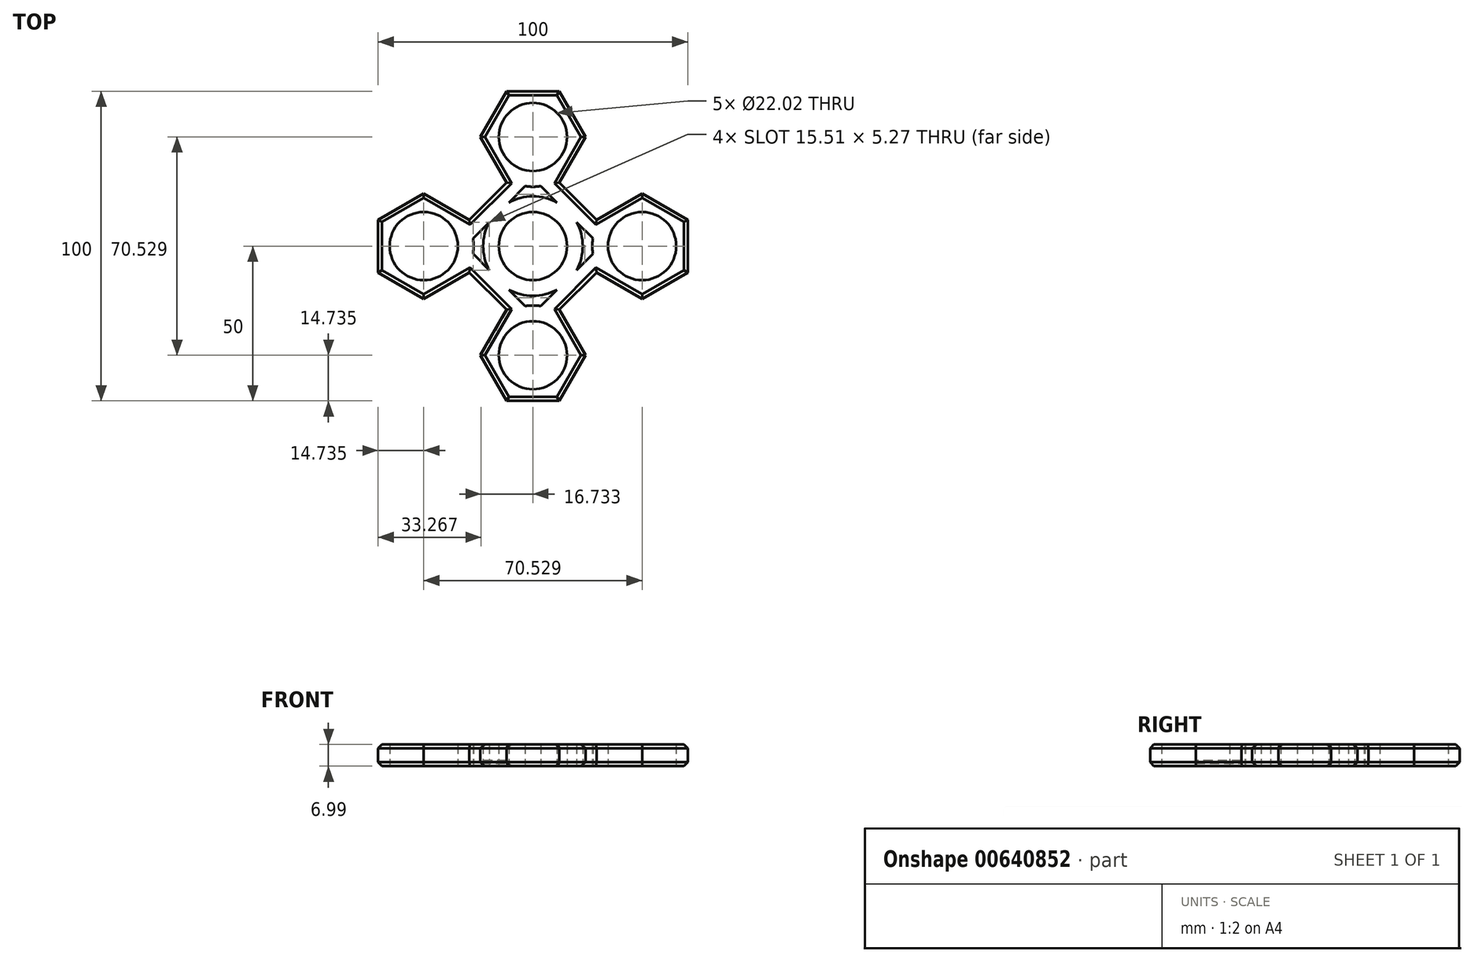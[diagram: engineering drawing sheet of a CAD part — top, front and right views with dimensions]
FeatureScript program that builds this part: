
annotation { "Feature Type Name" : "Feature", "Feature Type Description" : "" }
export const myFeature = defineFeature(function(context is Context, id is Id, definition is map)
    precondition{}
    {
        {
            var Q0;
            Q0=qCreatedBy(makeId("Top.planeOp"),FACE);
            var sketch = newSketch(context, id + "F0", { "sketchPlane" : qUnion([Q0])});
            skCircle(sketch, "E0", {"center": v(0, 0) * mm, "radius": 11.01 * mm});
            skCircle(sketch, "E1", {"center": v(0, 35.26) * mm, "radius": 11.01 * mm});
            skCircle(sketch, "E2", {"center": v(35.26, 0) * mm, "radius": 11.01 * mm});
            skCircle(sketch, "E3", {"center": v(0, -35.26) * mm, "radius": 11.01 * mm});
            skCircle(sketch, "E4", {"center": v(-35.26, 0) * mm, "radius": 11.01 * mm});
            skLineSegment(sketch, "E5", {"start": v(0, 0) * mm, "end": v(-35.26, 0) * mm});
            skLineSegment(sketch, "E6", {"start": v(0, 0) * mm, "end": v(0, 35.26) * mm});
            skLineSegment(sketch, "E7", {"start": v(0, 0) * mm, "end": v(35.26, 0) * mm});
            skLineSegment(sketch, "E8", {"start": v(0, 0) * mm, "end": v(0, -35.26) * mm});
            skCircle(sketch, "E9.cCircle", {"center": v(0, 0) * mm, "radius": 22.23 * mm, "construction": true});
            skLineSegment(sketch, "E9.0", {"start": v(-8.5, -20.53) * mm, "end": v(-20.53, -8.5) * mm});
            skLineSegment(sketch, "E9.1", {"start": v(-20.53, -8.5) * mm, "end": v(-20.53, 8.5) * mm});
            skLineSegment(sketch, "E9.2", {"start": v(-20.53, 8.5) * mm, "end": v(-8.5, 20.53) * mm});
            skLineSegment(sketch, "E9.3", {"start": v(-8.5, 20.53) * mm, "end": v(8.5, 20.53) * mm});
            skLineSegment(sketch, "E9.4", {"start": v(8.5, 20.53) * mm, "end": v(20.53, 8.5) * mm});
            skLineSegment(sketch, "E9.5", {"start": v(20.53, 8.5) * mm, "end": v(20.53, -8.5) * mm});
            skLineSegment(sketch, "E9.6", {"start": v(20.53, -8.5) * mm, "end": v(8.5, -20.53) * mm});
            skLineSegment(sketch, "E9.7", {"start": v(8.5, -20.53) * mm, "end": v(-8.5, -20.53) * mm});
            skCircle(sketch, "E10.cCircle", {"center": v(-35.26, 0) * mm, "radius": 17.01 * mm, "construction": true});
            skLineSegment(sketch, "E10.0", {"start": v(-20.53, -8.5) * mm, "end": v(-35.26, -17.01) * mm});
            skLineSegment(sketch, "E10.1", {"start": v(-35.26, -17.01) * mm, "end": v(-50, -8.5) * mm});
            skLineSegment(sketch, "E10.2", {"start": v(-50, -8.5) * mm, "end": v(-50, 8.5) * mm});
            skLineSegment(sketch, "E10.3", {"start": v(-50, 8.5) * mm, "end": v(-35.26, 17.01) * mm});
            skLineSegment(sketch, "E10.4", {"start": v(-35.26, 17.01) * mm, "end": v(-20.53, 8.5) * mm});
            skLineSegment(sketch, "E10.5", {"start": v(-20.53, 8.5) * mm, "end": v(-20.53, -8.5) * mm});
            skLineSegment(sketch, "E11.1", {"start": v(50, -9.14) * mm, "end": v(50, 7.87) * mm});
            skCircle(sketch, "E12.cCircle", {"center": v(35.26, 0) * mm, "radius": 17.01 * mm, "construction": true});
            skLineSegment(sketch, "E12.0", {"start": v(50, -8.5) * mm, "end": v(35.26, -17.01) * mm});
            skLineSegment(sketch, "E12.1", {"start": v(35.26, -17.01) * mm, "end": v(20.53, -8.5) * mm});
            skLineSegment(sketch, "E12.2", {"start": v(20.53, -8.5) * mm, "end": v(20.53, 8.5) * mm});
            skLineSegment(sketch, "E12.3", {"start": v(20.53, 8.5) * mm, "end": v(35.26, 17.01) * mm});
            skLineSegment(sketch, "E12.4", {"start": v(35.26, 17.01) * mm, "end": v(50, 8.5) * mm});
            skLineSegment(sketch, "E12.5", {"start": v(50, 8.5) * mm, "end": v(50, -8.5) * mm});
            skCircle(sketch, "E13.cCircle", {"center": v(0, -35.26) * mm, "radius": 17.01 * mm, "construction": true});
            skLineSegment(sketch, "E13.0", {"start": v(17.01, -35.26) * mm, "end": v(8.5, -50) * mm});
            skLineSegment(sketch, "E13.1", {"start": v(8.5, -50) * mm, "end": v(-8.5, -50) * mm});
            skLineSegment(sketch, "E13.2", {"start": v(-8.5, -50) * mm, "end": v(-17.01, -35.26) * mm});
            skLineSegment(sketch, "E13.3", {"start": v(-17.01, -35.26) * mm, "end": v(-8.5, -20.53) * mm});
            skLineSegment(sketch, "E13.4", {"start": v(-8.5, -20.53) * mm, "end": v(8.5, -20.53) * mm});
            skLineSegment(sketch, "E13.5", {"start": v(8.5, -20.53) * mm, "end": v(17.01, -35.26) * mm});
            skCircle(sketch, "E14.cCircle", {"center": v(0, 35.26) * mm, "radius": 17.01 * mm, "construction": true});
            skLineSegment(sketch, "E14.0", {"start": v(8.5, 20.53) * mm, "end": v(-8.5, 20.53) * mm});
            skLineSegment(sketch, "E14.1", {"start": v(-8.5, 20.53) * mm, "end": v(-17.01, 35.26) * mm});
            skLineSegment(sketch, "E14.2", {"start": v(-17.01, 35.26) * mm, "end": v(-8.5, 50) * mm});
            skLineSegment(sketch, "E14.3", {"start": v(-8.5, 50) * mm, "end": v(8.5, 50) * mm});
            skLineSegment(sketch, "E14.4", {"start": v(8.5, 50) * mm, "end": v(17.01, 35.26) * mm});
            skLineSegment(sketch, "E14.5", {"start": v(17.01, 35.26) * mm, "end": v(8.5, 20.53) * mm});
            skSolve(sketch);
        }
        {
            var Q0;
            Q0 = qSketchRegion(id + "F0", true);
            extrude(context, id + "F1", {"entities" : qUnion([Q0]), "depth" : 7 * mm, "offsetDistance" : 25.4 * mm});
        }
        {
            var Q0;
            Q0=makeQuery(id+"F1.opExtrude","CAP_FACE",FACE,{"disambiguationData":[OSD([sQuery(id+"F0.wireOp",EDGE,"E0"),sQuery(id+"F0.wireOp",EDGE,"E1"),sQuery(id+"F0.wireOp",EDGE,"E2"),sQuery(id+"F0.wireOp",EDGE,"E3"),sQuery(id+"F0.wireOp",EDGE,"E4"),sQuery(id+"F0.wireOp",EDGE,"E9.0"),sQuery(id+"F0.wireOp",EDGE,"E9.2"),sQuery(id+"F0.wireOp",EDGE,"E9.4"),sQuery(id+"F0.wireOp",EDGE,"E9.6"),sQuery(id+"F0.wireOp",EDGE,"E10.0"),sQuery(id+"F0.wireOp",EDGE,"E10.1"),sQuery(id+"F0.wireOp",EDGE,"E10.2"),sQuery(id+"F0.wireOp",EDGE,"E10.3"),sQuery(id+"F0.wireOp",EDGE,"E10.4"),sQuery(id+"F0.wireOp",EDGE,"E12.0"),sQuery(id+"F0.wireOp",EDGE,"E12.1"),sQuery(id+"F0.wireOp",EDGE,"E12.3"),sQuery(id+"F0.wireOp",EDGE,"E12.4"),sQuery(id+"F0.wireOp",EDGE,"E12.5"),sQuery(id+"F0.wireOp",EDGE,"E13.0"),sQuery(id+"F0.wireOp",EDGE,"E13.1"),sQuery(id+"F0.wireOp",EDGE,"E13.2"),sQuery(id+"F0.wireOp",EDGE,"E13.3"),sQuery(id+"F0.wireOp",EDGE,"E13.5"),sQuery(id+"F0.wireOp",EDGE,"E14.1"),sQuery(id+"F0.wireOp",EDGE,"E14.2"),sQuery(id+"F0.wireOp",EDGE,"E14.3"),sQuery(id+"F0.wireOp",EDGE,"E14.4"),sQuery(id+"F0.wireOp",EDGE,"E14.5")])],"isStart":true});
            var Q1;
            Q1=makeQuery(id+"F1.opExtrude","CAP_FACE",FACE,{"disambiguationData":[OSD([sQuery(id+"F0.wireOp",EDGE,"E0"),sQuery(id+"F0.wireOp",EDGE,"E1"),sQuery(id+"F0.wireOp",EDGE,"E2"),sQuery(id+"F0.wireOp",EDGE,"E3"),sQuery(id+"F0.wireOp",EDGE,"E4"),sQuery(id+"F0.wireOp",EDGE,"E9.0"),sQuery(id+"F0.wireOp",EDGE,"E9.2"),sQuery(id+"F0.wireOp",EDGE,"E9.4"),sQuery(id+"F0.wireOp",EDGE,"E9.6"),sQuery(id+"F0.wireOp",EDGE,"E10.0"),sQuery(id+"F0.wireOp",EDGE,"E10.1"),sQuery(id+"F0.wireOp",EDGE,"E10.2"),sQuery(id+"F0.wireOp",EDGE,"E10.3"),sQuery(id+"F0.wireOp",EDGE,"E10.4"),sQuery(id+"F0.wireOp",EDGE,"E12.0"),sQuery(id+"F0.wireOp",EDGE,"E12.1"),sQuery(id+"F0.wireOp",EDGE,"E12.3"),sQuery(id+"F0.wireOp",EDGE,"E12.4"),sQuery(id+"F0.wireOp",EDGE,"E12.5"),sQuery(id+"F0.wireOp",EDGE,"E13.0"),sQuery(id+"F0.wireOp",EDGE,"E13.1"),sQuery(id+"F0.wireOp",EDGE,"E13.2"),sQuery(id+"F0.wireOp",EDGE,"E13.3"),sQuery(id+"F0.wireOp",EDGE,"E13.5"),sQuery(id+"F0.wireOp",EDGE,"E14.1"),sQuery(id+"F0.wireOp",EDGE,"E14.2"),sQuery(id+"F0.wireOp",EDGE,"E14.3"),sQuery(id+"F0.wireOp",EDGE,"E14.4"),sQuery(id+"F0.wireOp",EDGE,"E14.5")])],"isStart":false});
            shell(context, id + "F2", {"entities" : qUnion([Q0, Q1]), "thickness" : 5.08 * mm});
        }
        {
            var Q0;
            Q0=makeQuery(id+"F1.opExtrude","CAP_EDGE",EDGE,{"disambiguationData":[OSD([sQuery(id+"F0.wireOp",EDGE,"E9.0")])],"isStart":false});
            var Q1;
            Q1=makeQuery(id+"F1.opExtrude","CAP_EDGE",EDGE,{"disambiguationData":[OSD([sQuery(id+"F0.wireOp",EDGE,"E9.2")])],"isStart":false});
            var Q2;
            Q2=makeQuery(id+"F1.opExtrude","CAP_EDGE",EDGE,{"disambiguationData":[OSD([sQuery(id+"F0.wireOp",EDGE,"E9.4")])],"isStart":false});
            var Q3;
            Q3=makeQuery(id+"F1.opExtrude","CAP_EDGE",EDGE,{"disambiguationData":[OSD([sQuery(id+"F0.wireOp",EDGE,"E9.6")])],"isStart":false});
            var Q4;
            Q4=makeQuery(id+"F1.opExtrude","CAP_EDGE",EDGE,{"disambiguationData":[OSD([sQuery(id+"F0.wireOp",EDGE,"E9.6")])],"isStart":true});
            var Q5;
            Q5=makeQuery(id+"F1.opExtrude","CAP_EDGE",EDGE,{"disambiguationData":[OSD([sQuery(id+"F0.wireOp",EDGE,"E9.4")])],"isStart":true});
            var Q6;
            Q6=makeQuery(id+"F1.opExtrude","CAP_EDGE",EDGE,{"disambiguationData":[OSD([sQuery(id+"F0.wireOp",EDGE,"E9.2")])],"isStart":true});
            var Q7;
            Q7=makeQuery(id+"F1.opExtrude","CAP_EDGE",EDGE,{"disambiguationData":[OSD([sQuery(id+"F0.wireOp",EDGE,"E9.0")])],"isStart":true});
            chamfer(context, id + "F3", {"entities" : qUnion([Q0, Q1, Q2, Q3, Q4, Q5, Q6, Q7]), "width" : 1.27 * mm, "tangentPropagation" : true});
        }
        {
            var Q0;
            Q0=makeQuery(id+"F1.opExtrude","CAP_EDGE",EDGE,{"disambiguationData":[OSD([sQuery(id+"F0.wireOp",EDGE,"E12.3")])],"isStart":true});
            var Q1;
            Q1=makeQuery(id+"F1.opExtrude","CAP_EDGE",EDGE,{"disambiguationData":[OSD([sQuery(id+"F0.wireOp",EDGE,"E12.1")])],"isStart":true});
            var Q2;
            Q2=makeQuery(id+"F1.opExtrude","CAP_EDGE",EDGE,{"disambiguationData":[OSD([sQuery(id+"F0.wireOp",EDGE,"E14.5")])],"isStart":true});
            var Q3;
            Q3=makeQuery(id+"F1.opExtrude","CAP_EDGE",EDGE,{"disambiguationData":[OSD([sQuery(id+"F0.wireOp",EDGE,"E14.1")])],"isStart":true});
            var Q4;
            Q4=makeQuery(id+"F1.opExtrude","CAP_EDGE",EDGE,{"disambiguationData":[OSD([sQuery(id+"F0.wireOp",EDGE,"E10.4")])],"isStart":true});
            var Q5;
            Q5=makeQuery(id+"F1.opExtrude","CAP_EDGE",EDGE,{"disambiguationData":[OSD([sQuery(id+"F0.wireOp",EDGE,"E10.0")])],"isStart":true});
            var Q6;
            Q6=makeQuery(id+"F1.opExtrude","CAP_EDGE",EDGE,{"disambiguationData":[OSD([sQuery(id+"F0.wireOp",EDGE,"E13.3")])],"isStart":true});
            var Q7;
            Q7=makeQuery(id+"F1.opExtrude","CAP_EDGE",EDGE,{"disambiguationData":[OSD([sQuery(id+"F0.wireOp",EDGE,"E13.5")])],"isStart":true});
            var Q8;
            Q8=makeQuery(id+"F1.opExtrude","CAP_EDGE",EDGE,{"disambiguationData":[OSD([sQuery(id+"F0.wireOp",EDGE,"E14.2")])],"isStart":true});
            var Q9;
            Q9=makeQuery(id+"F1.opExtrude","CAP_EDGE",EDGE,{"disambiguationData":[OSD([sQuery(id+"F0.wireOp",EDGE,"E14.4")])],"isStart":true});
            var Q10;
            Q10=makeQuery(id+"F1.opExtrude","CAP_EDGE",EDGE,{"disambiguationData":[OSD([sQuery(id+"F0.wireOp",EDGE,"E12.4")])],"isStart":true});
            var Q11;
            Q11=makeQuery(id+"F1.opExtrude","CAP_EDGE",EDGE,{"disambiguationData":[OSD([sQuery(id+"F0.wireOp",EDGE,"E13.0")])],"isStart":true});
            var Q12;
            Q12=makeQuery(id+"F1.opExtrude","CAP_EDGE",EDGE,{"disambiguationData":[OSD([sQuery(id+"F0.wireOp",EDGE,"E13.1")])],"isStart":true});
            var Q13;
            Q13=makeQuery(id+"F1.opExtrude","CAP_EDGE",EDGE,{"disambiguationData":[OSD([sQuery(id+"F0.wireOp",EDGE,"E13.2")])],"isStart":true});
            var Q14;
            Q14=makeQuery(id+"F1.opExtrude","CAP_EDGE",EDGE,{"disambiguationData":[OSD([sQuery(id+"F0.wireOp",EDGE,"E10.1")])],"isStart":true});
            var Q15;
            Q15=makeQuery(id+"F1.opExtrude","CAP_EDGE",EDGE,{"disambiguationData":[OSD([sQuery(id+"F0.wireOp",EDGE,"E10.2")])],"isStart":true});
            var Q16;
            Q16=makeQuery(id+"F1.opExtrude","CAP_EDGE",EDGE,{"disambiguationData":[OSD([sQuery(id+"F0.wireOp",EDGE,"E10.3")])],"isStart":true});
            var Q17;
            Q17=makeQuery(id+"F1.opExtrude","CAP_EDGE",EDGE,{"disambiguationData":[OSD([sQuery(id+"F0.wireOp",EDGE,"E14.3")])],"isStart":true});
            var Q18;
            Q18=makeQuery(id+"F1.opExtrude","CAP_EDGE",EDGE,{"disambiguationData":[OSD([sQuery(id+"F0.wireOp",EDGE,"E12.5")])],"isStart":true});
            var Q19;
            Q19=makeQuery(id+"F1.opExtrude","CAP_EDGE",EDGE,{"disambiguationData":[OSD([sQuery(id+"F0.wireOp",EDGE,"E12.0")])],"isStart":true});
            chamfer(context, id + "F4", {"entities" : qUnion([Q0, Q1, Q2, Q3, Q4, Q5, Q6, Q7, Q8, Q9, Q10, Q11, Q12, Q13, Q14, Q15, Q16, Q17, Q18, Q19]), "width" : 1.27 * mm, "tangentPropagation" : true});
        }
        {
            var Q0;
            Q0=makeQuery(id+"F1.opExtrude","CAP_EDGE",EDGE,{"disambiguationData":[OSD([sQuery(id+"F0.wireOp",EDGE,"E14.3")])],"isStart":false});
            var Q1;
            Q1=makeQuery(id+"F1.opExtrude","CAP_EDGE",EDGE,{"disambiguationData":[OSD([sQuery(id+"F0.wireOp",EDGE,"E10.2")])],"isStart":false});
            var Q2;
            Q2=makeQuery(id+"F1.opExtrude","CAP_EDGE",EDGE,{"disambiguationData":[OSD([sQuery(id+"F0.wireOp",EDGE,"E13.1")])],"isStart":false});
            var Q3;
            Q3=makeQuery(id+"F1.opExtrude","CAP_EDGE",EDGE,{"disambiguationData":[OSD([sQuery(id+"F0.wireOp",EDGE,"E12.5")])],"isStart":false});
            var Q4;
            Q4=makeQuery(id+"F1.opExtrude","CAP_EDGE",EDGE,{"disambiguationData":[OSD([sQuery(id+"F0.wireOp",EDGE,"E14.4")])],"isStart":false});
            var Q5;
            Q5=makeQuery(id+"F1.opExtrude","CAP_EDGE",EDGE,{"disambiguationData":[OSD([sQuery(id+"F0.wireOp",EDGE,"E14.2")])],"isStart":false});
            var Q6;
            Q6=makeQuery(id+"F1.opExtrude","CAP_EDGE",EDGE,{"disambiguationData":[OSD([sQuery(id+"F0.wireOp",EDGE,"E10.3")])],"isStart":false});
            var Q7;
            Q7=makeQuery(id+"F1.opExtrude","CAP_EDGE",EDGE,{"disambiguationData":[OSD([sQuery(id+"F0.wireOp",EDGE,"E10.1")])],"isStart":false});
            var Q8;
            Q8=makeQuery(id+"F1.opExtrude","CAP_EDGE",EDGE,{"disambiguationData":[OSD([sQuery(id+"F0.wireOp",EDGE,"E13.2")])],"isStart":false});
            var Q9;
            Q9=makeQuery(id+"F1.opExtrude","CAP_EDGE",EDGE,{"disambiguationData":[OSD([sQuery(id+"F0.wireOp",EDGE,"E13.0")])],"isStart":false});
            var Q10;
            Q10=makeQuery(id+"F1.opExtrude","CAP_EDGE",EDGE,{"disambiguationData":[OSD([sQuery(id+"F0.wireOp",EDGE,"E12.0")])],"isStart":false});
            var Q11;
            Q11=makeQuery(id+"F1.opExtrude","CAP_EDGE",EDGE,{"disambiguationData":[OSD([sQuery(id+"F0.wireOp",EDGE,"E12.4")])],"isStart":false});
            chamfer(context, id + "F5", {"entities" : qUnion([Q0, Q1, Q2, Q3, Q4, Q5, Q6, Q7, Q8, Q9, Q10, Q11]), "width" : 1.27 * mm, "tangentPropagation" : true});
        }
        {
            var Q0;
            Q0=makeQuery(id+"F1.opExtrude","CAP_EDGE",EDGE,{"disambiguationData":[OSD([sQuery(id+"F0.wireOp",EDGE,"E13.5")])],"isStart":false});
            var Q1;
            {var subQ0=sQuery(id+"F0.wireOp",EDGE,"E13.3");Q1=makeQuery(id+"F4.opChamfer","BLEND_EDGE",EDGE,{"blendedFrom":[makeQuery(id+"F1.opExtrude","CAP_EDGE",EDGE,{"disambiguationData":[OSD([subQ0])],"isStart":true}),makeQuery(id+"F1.opExtrude","SWEPT_FACE",FACE,{"disambiguationData":[OSD([subQ0])]})],"blendedInto":[makeQuery(id+"F1.opExtrude","SWEPT_FACE",FACE,{"disambiguationData":[OSD([subQ0])]})]});}
            var Q2;
            Q2=makeQuery(id+"F1.opExtrude","CAP_EDGE",EDGE,{"disambiguationData":[OSD([sQuery(id+"F0.wireOp",EDGE,"E10.0")])],"isStart":false});
            var Q3;
            Q3=makeQuery(id+"F1.opExtrude","CAP_EDGE",EDGE,{"disambiguationData":[OSD([sQuery(id+"F0.wireOp",EDGE,"E10.4")])],"isStart":false});
            var Q4;
            Q4=makeQuery(id+"F1.opExtrude","CAP_EDGE",EDGE,{"disambiguationData":[OSD([sQuery(id+"F0.wireOp",EDGE,"E14.1")])],"isStart":false});
            var Q5;
            Q5=makeQuery(id+"F1.opExtrude","CAP_EDGE",EDGE,{"disambiguationData":[OSD([sQuery(id+"F0.wireOp",EDGE,"E14.5")])],"isStart":false});
            var Q6;
            Q6=makeQuery(id+"F1.opExtrude","CAP_EDGE",EDGE,{"disambiguationData":[OSD([sQuery(id+"F0.wireOp",EDGE,"E12.3")])],"isStart":false});
            var Q7;
            Q7=makeQuery(id+"F1.opExtrude","CAP_EDGE",EDGE,{"disambiguationData":[OSD([sQuery(id+"F0.wireOp",EDGE,"E12.1")])],"isStart":false});
            var Q8;
            Q8=makeQuery(id+"F1.opExtrude","CAP_EDGE",EDGE,{"disambiguationData":[OSD([sQuery(id+"F0.wireOp",EDGE,"E13.3")])],"isStart":false});
            chamfer(context, id + "F6", {"entities" : qUnion([Q0, Q1, Q2, Q3, Q4, Q5, Q6, Q7, Q8]), "width" : 1.27 * mm, "tangentPropagation" : true});
        }
    });
